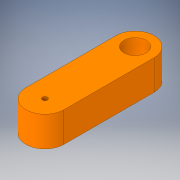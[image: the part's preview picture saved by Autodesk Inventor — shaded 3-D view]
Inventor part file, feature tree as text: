
AUTODESK INVENTOR PART (.ipt)
format: ipt  version: 2017 (Build 210142000, 142)  size: 115,712 bytes
history: native  units: in
note: dims shown in document units (in); Inventor stores cm internally (conversion verified against a paired STEP export)
features: extrude x1, sketch x1
ambient origin geometry x8: Origin, YZ Plane, XZ Plane, XY Plane, X Axis, Y Axis, Z Axis, Center Point
bodies: Solid1 (feature_tree)
feature tree (2):
  extrude  "Extrusion1"  Depth=0.748in
  sketch  "Sketch1"  dims[d0=1.4961in d2=0.748in d3=0.1969in d4=0.8661in d6=0.0in]
